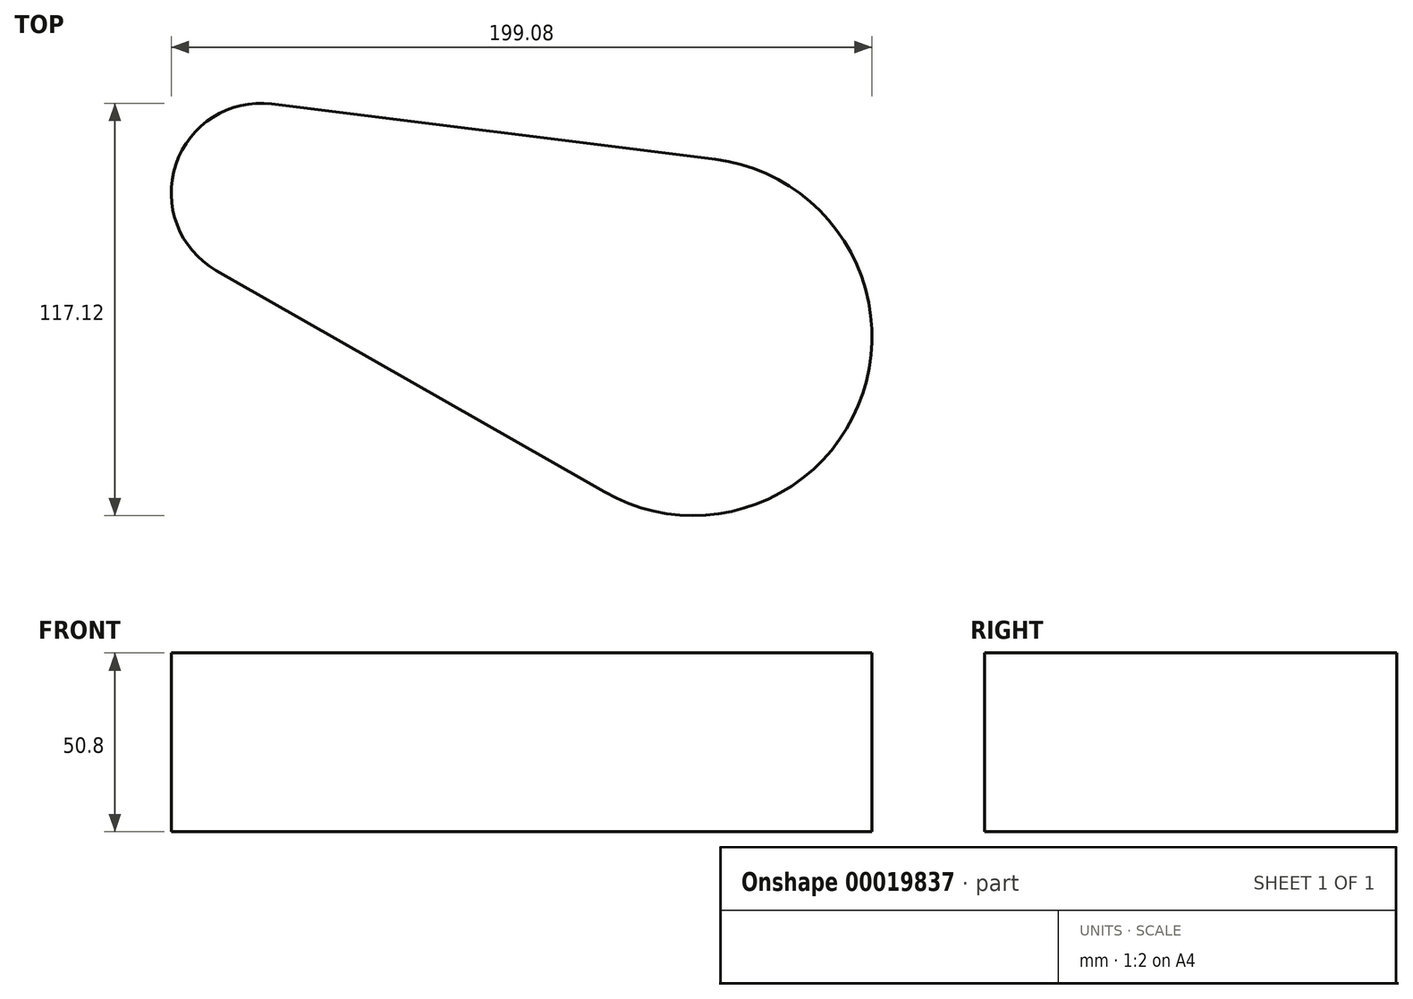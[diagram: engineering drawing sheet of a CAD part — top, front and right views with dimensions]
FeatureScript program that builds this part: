
annotation { "Feature Type Name" : "Feature", "Feature Type Description" : "" }
export const myFeature = defineFeature(function(context is Context, id is Id, definition is map)
    precondition{}
    {
        {
            var Q0;
            Q0=qCreatedBy(makeId("Top.planeOp"),FACE);
            var sketch = newSketch(context, id + "F0", { "sketchPlane" : qUnion([Q0])});
            skCircle(sketch, "E0", {"center": v(0, 0) * mm, "radius": 50.8 * mm});
            skCircle(sketch, "E1", {"center": v(-122.88, 40.92) * mm, "radius": 25.4 * mm});
            skLineSegment(sketch, "E2", {"start": v(-119.74, 66.13) * mm, "end": v(6.29, 50.4) * mm});
            skLineSegment(sketch, "E3", {"start": v(-135.48, 18.87) * mm, "end": v(-25.2, -44.11) * mm});
            skSolve(sketch);
        }
        {
            var Q0;
            {var subQ0=sQuery(id+"F0.wireOp",EDGE,"E0");var subQ2=makeQuery(id+"F0.imprint","INTERSECT",VERTEX,{"derivedFrom":[subQ0,sQuery(id+"F0.wireOp",EDGE,"E2")]});Q0=makeQuery(id+"F0.imprint","IMPRINT",FACE,{"disambiguationData":[TD([[makeQuery(id+"F0.imprint","IMPRINT",EDGE,{"disambiguationData":[TD([[subQ2,-1.0]])],"derivedFrom":subQ0}),1.0]])]});}
            var Q1;
            {var subQ1=sQuery(id+"F0.wireOp",EDGE,"E2");Q1=makeQuery(id+"F0.imprint","IMPRINT",FACE,{"disambiguationData":[TD([[makeQuery(id+"F0.imprint","IMPRINT",EDGE,{"derivedFrom":subQ1}),-1.0]])]});}
            var Q2;
            {var subQ0=sQuery(id+"F0.wireOp",EDGE,"E1");var subQ2=makeQuery(id+"F0.imprint","INTERSECT",VERTEX,{"derivedFrom":[subQ0,sQuery(id+"F0.wireOp",EDGE,"E2")]});Q2=makeQuery(id+"F0.imprint","IMPRINT",FACE,{"disambiguationData":[TD([[makeQuery(id+"F0.imprint","IMPRINT",EDGE,{"disambiguationData":[TD([[subQ2,-1.0]])],"derivedFrom":subQ0}),1.0]])]});}
            extrude(context, id + "F1", {"entities" : qUnion([Q0, Q1, Q2]), "depth" : 50.8 * mm});
        }
    });
